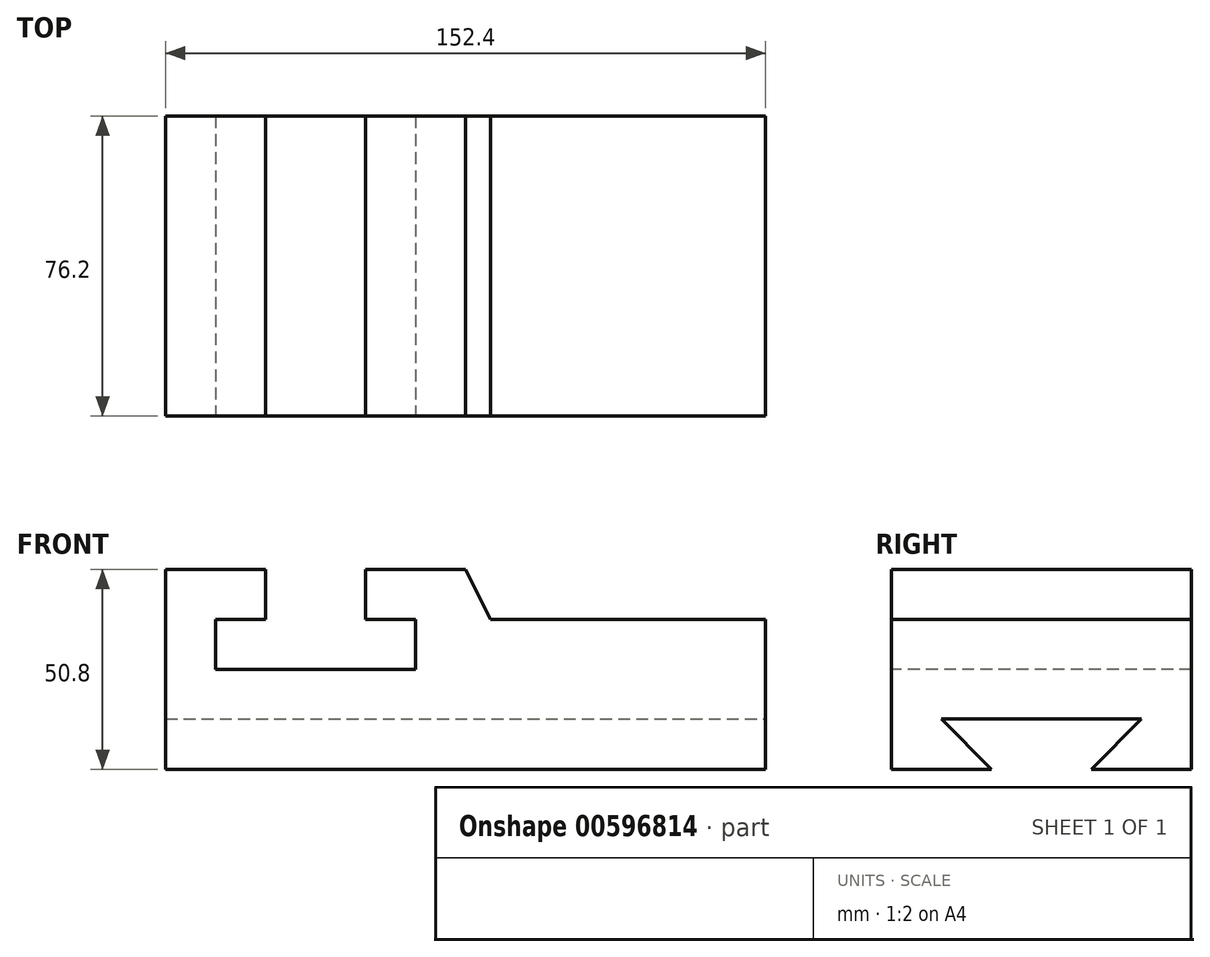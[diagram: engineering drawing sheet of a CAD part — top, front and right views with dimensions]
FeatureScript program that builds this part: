
annotation { "Feature Type Name" : "Feature", "Feature Type Description" : "" }
export const myFeature = defineFeature(function(context is Context, id is Id, definition is map)
    precondition{}
    {
        {
            var Q0;
            Q0=qCreatedBy(makeId("Front.planeOp"),FACE);
            var sketch = newSketch(context, id + "F0", { "sketchPlane" : qUnion([Q0])});
            skLineSegment(sketch, "E0.bottom", {"start": v(0, 0) * mm, "end": v(-152.4, 0) * mm});
            skLineSegment(sketch, "E0.top", {"start": v(0, 50.8) * mm, "end": v(-152.4, 50.8) * mm});
            skLineSegment(sketch, "E0.left", {"start": v(0, 0) * mm, "end": v(0, 50.8) * mm});
            skLineSegment(sketch, "E0.right", {"start": v(-152.4, 0) * mm, "end": v(-152.4, 50.8) * mm});
            skSolve(sketch);
        }
        {
            var Q0;
            Q0=makeQuery(id+"F0.imprint","IMPRINT",FACE,{"disambiguationData":[TD([[makeQuery(id+"F0.imprint","IMPRINT",EDGE,{"derivedFrom":sQuery(id+"F0.wireOp",EDGE,"E0.bottom")}),-1.0]])]});
            extrude(context, id + "F1", {"entities" : qUnion([Q0]), "depth" : 76.2 * mm, "offsetDistance" : 25.4 * mm});
        }
        {
            var Q0;
            Q0=makeQuery(id+"F1.opExtrude","CAP_FACE",FACE,{"disambiguationData":[OSD([sQuery(id+"F0.wireOp",EDGE,"E0.bottom"),sQuery(id+"F0.wireOp",EDGE,"E0.top"),sQuery(id+"F0.wireOp",EDGE,"E0.left"),sQuery(id+"F0.wireOp",EDGE,"E0.right")])],"isStart":false});
            var sketch = newSketch(context, id + "F2", { "sketchPlane" : qUnion([Q0])});
            skLineSegment(sketch, "E1", {"start": v(-152.4, 50.8) * mm, "end": v(-127, 50.8) * mm});
            skLineSegment(sketch, "E2", {"start": v(-127, 50.8) * mm, "end": v(-127, 38.1) * mm});
            skLineSegment(sketch, "E3", {"start": v(-127, 38.1) * mm, "end": v(-139.7, 38.1) * mm});
            skLineSegment(sketch, "E4", {"start": v(-139.7, 38.1) * mm, "end": v(-139.7, 25.4) * mm});
            skLineSegment(sketch, "E5", {"start": v(-139.7, 25.4) * mm, "end": v(-88.9, 25.4) * mm});
            skLineSegment(sketch, "E6", {"start": v(-88.9, 25.4) * mm, "end": v(-88.9, 38.1) * mm});
            skLineSegment(sketch, "E7", {"start": v(-88.9, 38.1) * mm, "end": v(-101.6, 38.1) * mm});
            skLineSegment(sketch, "E8", {"start": v(-101.6, 38.1) * mm, "end": v(-101.6, 50.8) * mm});
            skLineSegment(sketch, "E9", {"start": v(-127, 50.8) * mm, "end": v(-101.6, 50.8) * mm});
            skSolve(sketch);
        }
        {
            var Q0;
            Q0=makeQuery(id+"F2.imprint","IMPRINT",FACE,{"disambiguationData":[TD([[makeQuery(id+"F2.imprint","IMPRINT",EDGE,{"derivedFrom":sQuery(id+"F2.wireOp",EDGE,"E2")}),1.0]])]});
            extrude(context, id + "F3", {"entities" : qUnion([Q0]), "operationType" : NewBodyOperationType.REMOVE, "oppositeDirection" : true, "depth" : 92.96 * mm, "offsetDistance" : 25.4 * mm});
        }
        {
            var Q0;
            Q0=makeQuery(id+"F1.opExtrude","CAP_FACE",FACE,{"disambiguationData":[OSD([sQuery(id+"F0.wireOp",EDGE,"E0.bottom"),sQuery(id+"F0.wireOp",EDGE,"E0.top"),sQuery(id+"F0.wireOp",EDGE,"E0.left"),sQuery(id+"F0.wireOp",EDGE,"E0.right")])],"isStart":false});
            var sketch = newSketch(context, id + "F4", { "sketchPlane" : qUnion([Q0])});
            skLineSegment(sketch, "E10", {"start": v(-101.6, 50.8) * mm, "end": v(-76.2, 50.8) * mm});
            skLineSegment(sketch, "E11", {"start": v(-76.2, 50.8) * mm, "end": v(-69.85, 38.1) * mm});
            skLineSegment(sketch, "E12", {"start": v(-69.85, 38.1) * mm, "end": v(0, 38.1) * mm});
            skLineSegment(sketch, "E13", {"start": v(-76.2, 50.8) * mm, "end": v(0, 50.8) * mm});
            skLineSegment(sketch, "E14", {"start": v(0, 50.8) * mm, "end": v(0, 38.1) * mm});
            skSolve(sketch);
        }
        {
            var Q0;
            Q0=makeQuery(id+"F4.imprint","IMPRINT",FACE,{"disambiguationData":[TD([[makeQuery(id+"F4.imprint","IMPRINT",EDGE,{"derivedFrom":sQuery(id+"F4.wireOp",EDGE,"E11")}),1.0]])]});
            extrude(context, id + "F5", {"entities" : qUnion([Q0]), "operationType" : NewBodyOperationType.REMOVE, "oppositeDirection" : true, "depth" : 93.47 * mm, "offsetDistance" : 25.4 * mm});
        }
        {
            var Q0;
            Q0=makeQuery(id+"F1.opExtrude","SWEPT_FACE",FACE,{"disambiguationData":[OSD([sQuery(id+"F0.wireOp",EDGE,"E0.left")])]});
            var sketch = newSketch(context, id + "F6", { "sketchPlane" : qUnion([Q0])});
            skLineSegment(sketch, "E15", {"start": v(-76.2, 0) * mm, "end": v(-50.8, 0) * mm});
            skPoint(sketch, "E16.endSnap0", {"position": v(-63.5, 0) * mm});
            skLineSegment(sketch, "E17", {"start": v(-63.5, 12.83) * mm, "end": v(-12.7, 12.83) * mm});
            skLineSegment(sketch, "E18", {"start": v(-50.8, 0) * mm, "end": v(-63.5, 12.83) * mm});
            skLineSegment(sketch, "E19", {"start": v(0, 0) * mm, "end": v(-25.4, 0) * mm});
            skLineSegment(sketch, "E20", {"start": v(-12.7, 12.83) * mm, "end": v(-25.4, 0) * mm});
            skSolve(sketch);
        }
        {
            var Q0;
            Q0=makeQuery(id+"F6.imprint","IMPRINT",FACE,{"disambiguationData":[TD([[makeQuery(id+"F6.imprint","IMPRINT",EDGE,{"derivedFrom":sQuery(id+"F6.wireOp",EDGE,"E17")}),-1.0]])]});
            extrude(context, id + "F7", {"entities" : qUnion([Q0]), "operationType" : NewBodyOperationType.REMOVE, "oppositeDirection" : true, "depth" : 203.45 * mm, "offsetDistance" : 25.4 * mm});
        }
    });
